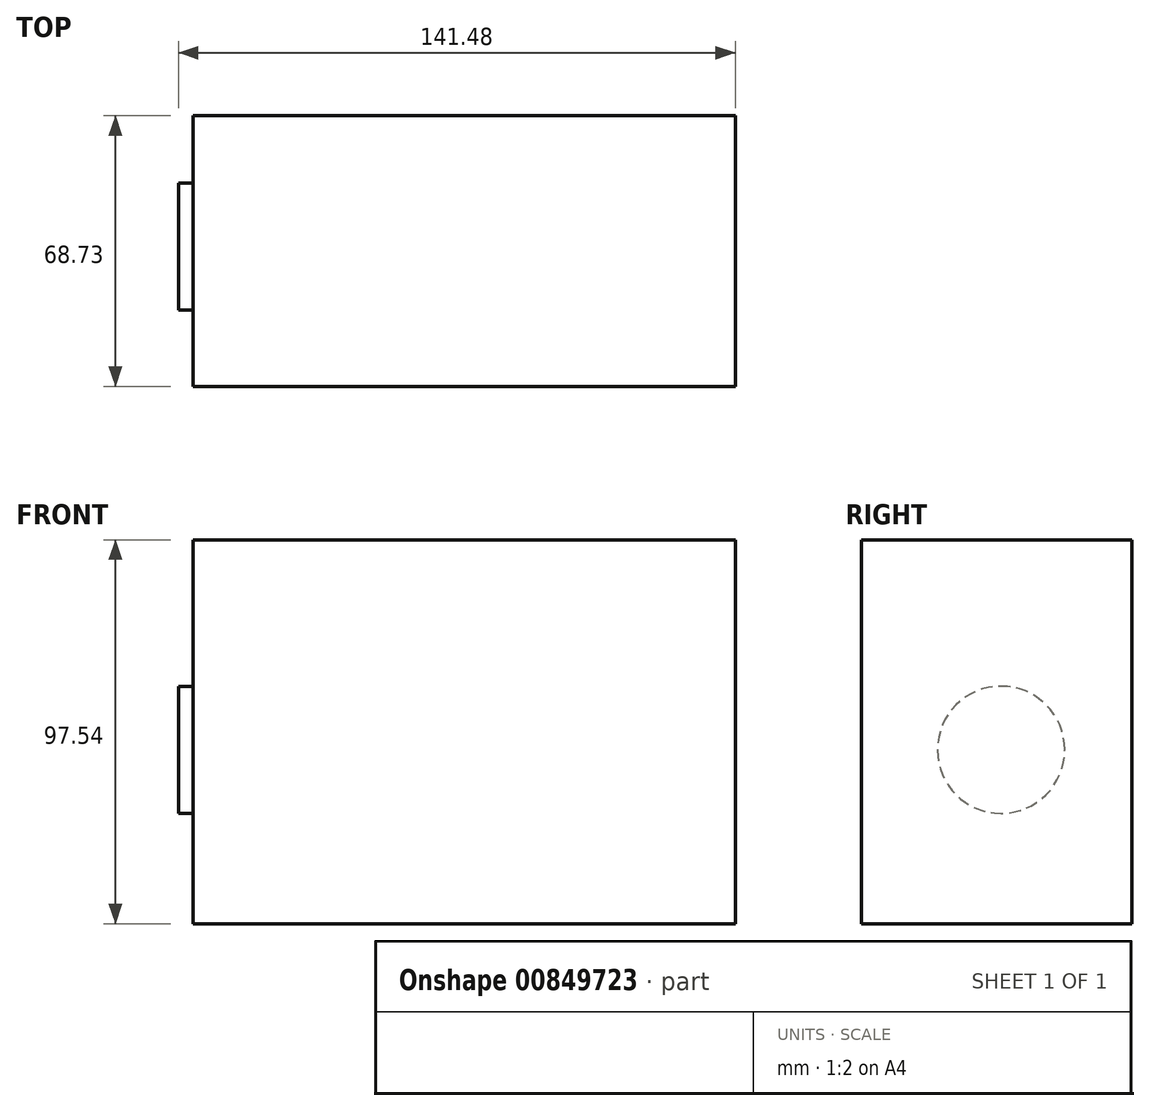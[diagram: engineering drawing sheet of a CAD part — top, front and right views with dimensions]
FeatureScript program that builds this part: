
annotation { "Feature Type Name" : "Feature", "Feature Type Description" : "" }
export const myFeature = defineFeature(function(context is Context, id is Id, definition is map)
    precondition{}
    {
        {
            var Q0;
            Q0=qCreatedBy(makeId("Top.planeOp"),FACE);
            var sketch = newSketch(context, id + "F0", { "sketchPlane" : qUnion([Q0])});
            skLineSegment(sketch, "E0.bottom", {"start": v(0, 0) * mm, "end": v(137.72, 0) * mm});
            skLineSegment(sketch, "E0.top", {"start": v(0, -68.73) * mm, "end": v(137.72, -68.73) * mm});
            skLineSegment(sketch, "E0.left", {"start": v(0, 0) * mm, "end": v(0, -68.73) * mm});
            skLineSegment(sketch, "E0.right", {"start": v(137.72, 0) * mm, "end": v(137.72, -68.73) * mm});
            skSolve(sketch);
        }
        {
            var Q0;
            Q0 = qSketchRegion(id + "F0", true);
            extrude(context, id + "F1", {"entities" : qUnion([Q0]), "depth" : 97.54 * mm, "offsetDistance" : 25.4 * mm});
        }
        {
            var Q0;
            Q0=makeQuery(id+"F1.opExtrude","SWEPT_FACE",FACE,{"disambiguationData":[OSD([sQuery(id+"F0.wireOp",EDGE,"E0.right")])]});
            var sketch = newSketch(context, id + "F2", { "sketchPlane" : qUnion([Q0])});
            skCircle(sketch, "E1", {"center": v(-33.2, 44.19) * mm, "radius": 16.16 * mm});
            skSolve(sketch);
        }
        {
            var Q0;
            Q0 = qSketchRegion(id + "F2", true);
            extrude(context, id + "F3", {"entities" : qUnion([Q0]), "operationType" : NewBodyOperationType.ADD, "oppositeDirection" : true, "depth" : 141.48 * mm, "offsetDistance" : 25.4 * mm});
        }
    });
